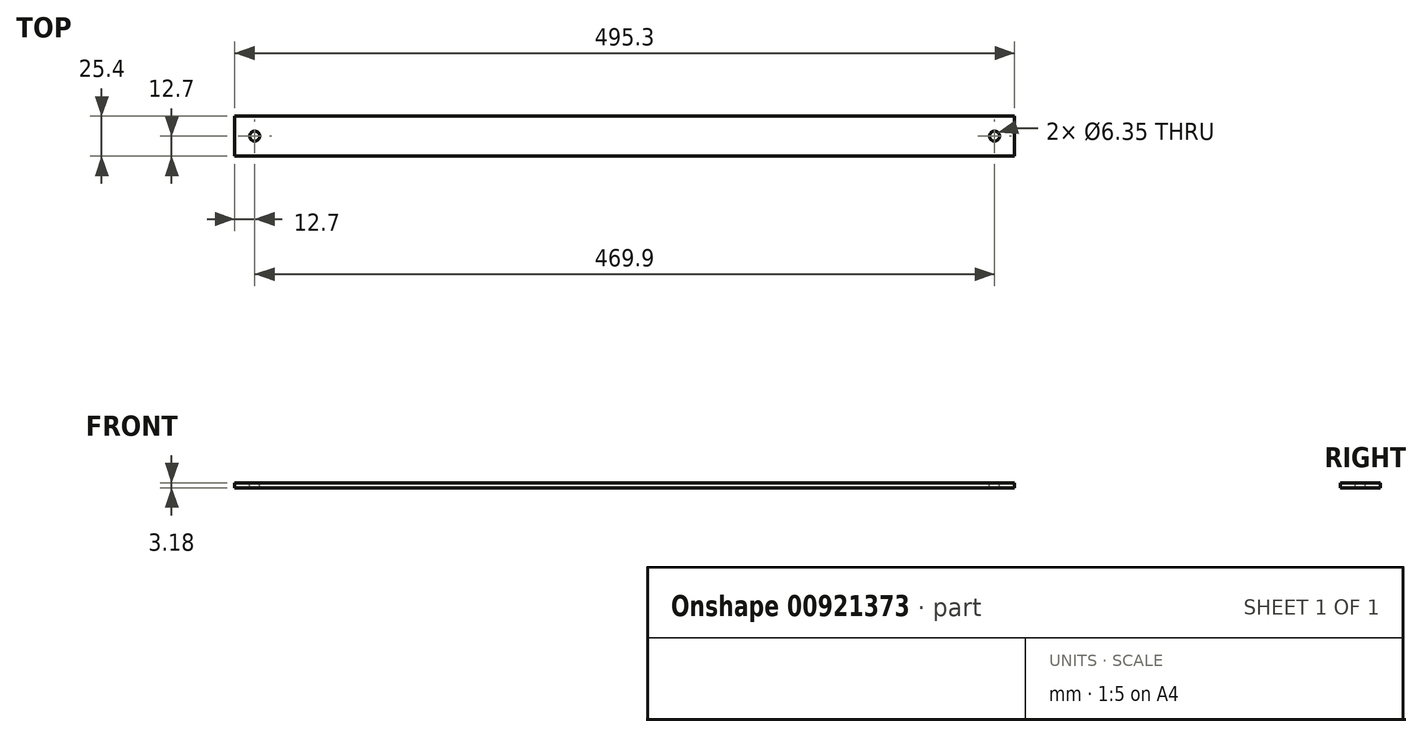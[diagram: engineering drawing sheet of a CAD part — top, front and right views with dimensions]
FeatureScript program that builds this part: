
annotation { "Feature Type Name" : "Feature", "Feature Type Description" : "" }
export const myFeature = defineFeature(function(context is Context, id is Id, definition is map)
    precondition{}
    {
        {
            var Q0;
            Q0=qCreatedBy(makeId("Right.planeOp"),FACE);
            var sketch = newSketch(context, id + "F0", { "sketchPlane" : qUnion([Q0])});
            skLineSegment(sketch, "E0.bottom", {"start": v(-12.7, 1.59) * mm, "end": v(12.7, 1.59) * mm});
            skLineSegment(sketch, "E0.top", {"start": v(-12.7, -1.59) * mm, "end": v(12.7, -1.59) * mm});
            skLineSegment(sketch, "E0.left", {"start": v(-12.7, 1.59) * mm, "end": v(-12.7, -1.59) * mm});
            skLineSegment(sketch, "E0.right", {"start": v(12.7, 1.59) * mm, "end": v(12.7, -1.59) * mm});
            skLineSegment(sketch, "E1", {"start": v(-12.7, 1.59) * mm, "end": v(12.7, -1.59) * mm, "construction": true});
            skSolve(sketch);
        }
        {
            var Q0;
            Q0 = qSketchRegion(id + "F0", true);
            extrude(context, id + "F1", {"entities" : qUnion([Q0]), "endBound" : BoundingType.SYMMETRIC, "depth" : 495.3 * mm, "offsetDistance" : 25.4 * mm});
        }
        {
            var Q0;
            Q0=makeQuery(id+"F1.opExtrude","SWEPT_FACE",FACE,{"disambiguationData":[OSD([sQuery(id+"F0.wireOp",EDGE,"E0.bottom")])]});
            var sketch = newSketch(context, id + "F2", { "sketchPlane" : qUnion([Q0])});
            skLineSegment(sketch, "E2", {"start": v(-247.65, 0) * mm, "end": v(247.65, 0) * mm, "construction": true});
            skCircle(sketch, "E3", {"center": v(234.95, 0) * mm, "radius": 3.18 * mm});
            skCircle(sketch, "E4", {"center": v(-234.95, 0) * mm, "radius": 3.18 * mm});
            skSolve(sketch);
        }
        {
            var Q0;
            Q0 = qSketchRegion(id + "F2", true);
            extrude(context, id + "F3", {"entities" : qUnion([Q0]), "operationType" : NewBodyOperationType.REMOVE, "endBound" : BoundingType.THROUGH_ALL, "oppositeDirection" : true, "depth" : 25.4 * mm, "offsetDistance" : 25.4 * mm});
        }
    });
